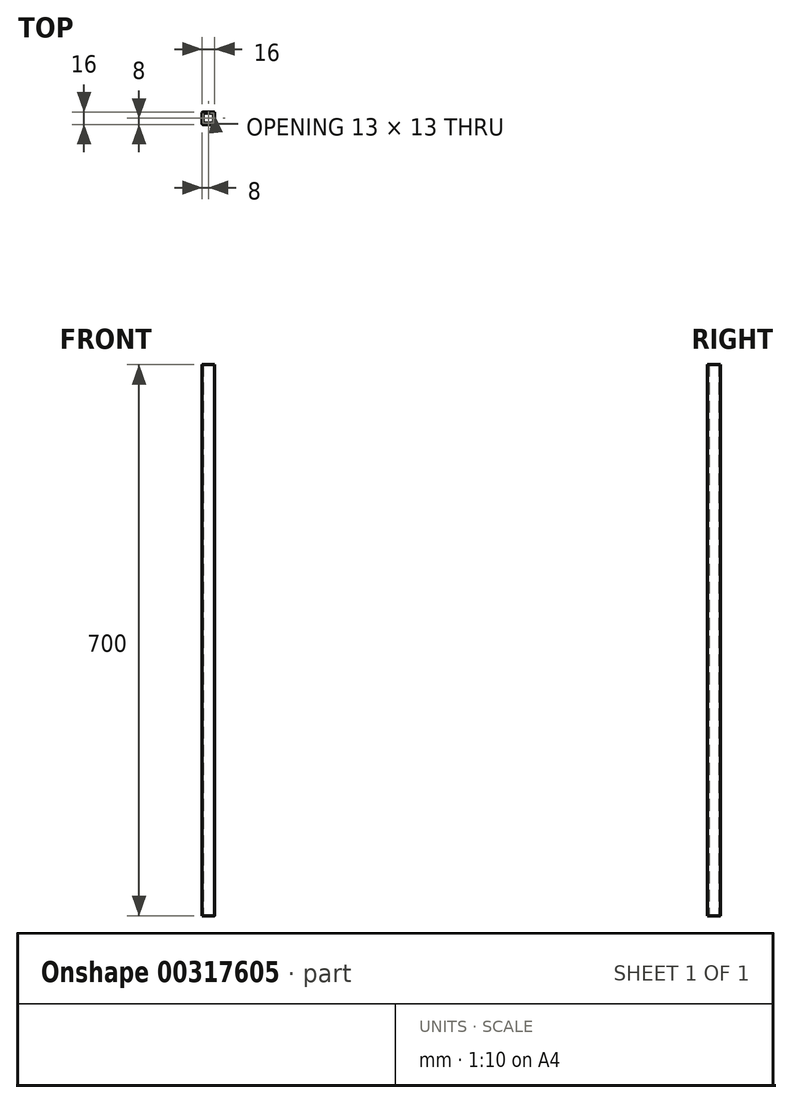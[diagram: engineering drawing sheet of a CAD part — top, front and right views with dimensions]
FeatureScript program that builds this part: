
annotation { "Feature Type Name" : "Feature", "Feature Type Description" : "" }
export const myFeature = defineFeature(function(context is Context, id is Id, definition is map)
    precondition{}
    {
        {
            var Q0;
            Q0=qCreatedBy(makeId("Top.planeOp"),FACE);
            var sketch = newSketch(context, id + "F0", { "sketchPlane" : qUnion([Q0])});
            skLineSegment(sketch, "E0.bottom", {"start": v(-8, -8) * mm, "end": v(8, -8) * mm});
            skLineSegment(sketch, "E0.top", {"start": v(-8, 8) * mm, "end": v(8, 8) * mm});
            skLineSegment(sketch, "E0.left", {"start": v(-8, -8) * mm, "end": v(-8, 8) * mm});
            skLineSegment(sketch, "E0.right", {"start": v(8, -8) * mm, "end": v(8, 8) * mm});
            skSolve(sketch);
        }
        {
            var Q0;
            Q0=makeQuery(id+"F0.imprint","IMPRINT",FACE,{"disambiguationData":[TD([[makeQuery(id+"F0.imprint","IMPRINT",EDGE,{"derivedFrom":sQuery(id+"F0.wireOp",EDGE,"E0.bottom")}),1.0]])]});
            extrude(context, id + "F1", {"entities" : qUnion([Q0]), "depth" : 700 * mm});
        }
        {
            var Q0;
            Q0=makeQuery(id+"F1.opExtrude","CAP_FACE",FACE,{"disambiguationData":[OSD([sQuery(id+"F0.wireOp",EDGE,"E0.bottom"),sQuery(id+"F0.wireOp",EDGE,"E0.top"),sQuery(id+"F0.wireOp",EDGE,"E0.left"),sQuery(id+"F0.wireOp",EDGE,"E0.right")])],"isStart":false});
            var Q1;
            Q1=makeQuery(id+"F1.opExtrude","CAP_FACE",FACE,{"disambiguationData":[OSD([sQuery(id+"F0.wireOp",EDGE,"E0.bottom"),sQuery(id+"F0.wireOp",EDGE,"E0.top"),sQuery(id+"F0.wireOp",EDGE,"E0.left"),sQuery(id+"F0.wireOp",EDGE,"E0.right")])],"isStart":true});
            shell(context, id + "F2", {"entities" : qUnion([Q0, Q1]), "thickness" : 1.5 * mm});
        }
        {
            var Q0;
            Q0=makeQuery(id+"F1.opExtrude","SWEPT_EDGE",EDGE,{"disambiguationData":[OSD([sQuery(id+"F0.wireOp",EDGE,"E0.top"),sQuery(id+"F0.wireOp",EDGE,"E0.left")])]});
            var Q1;
            Q1=makeQuery(id+"F1.opExtrude","SWEPT_EDGE",EDGE,{"disambiguationData":[OSD([sQuery(id+"F0.wireOp",EDGE,"E0.top"),sQuery(id+"F0.wireOp",EDGE,"E0.right")])]});
            var Q2;
            Q2=makeQuery(id+"F1.opExtrude","SWEPT_EDGE",EDGE,{"disambiguationData":[OSD([sQuery(id+"F0.wireOp",EDGE,"E0.bottom"),sQuery(id+"F0.wireOp",EDGE,"E0.right")])]});
            var Q3;
            Q3=makeQuery(id+"F1.opExtrude","SWEPT_EDGE",EDGE,{"disambiguationData":[OSD([sQuery(id+"F0.wireOp",EDGE,"E0.bottom"),sQuery(id+"F0.wireOp",EDGE,"E0.left")])]});
            fillet(context, id + "F3", {"entities" : qUnion([Q0, Q1, Q2, Q3]), "radius" : 1.5 * mm, "tangentPropagation" : true, "allowEdgeOverflow" : false});
        }
        {
            var Q0;
            Q0=makeQuery(id+"F2.opShell","OFFSET_EDGE",EDGE,{"disambiguationData":[OSD([sQuery(id+"F0.wireOp",EDGE,"E0.top"),sQuery(id+"F0.wireOp",EDGE,"E0.right")])]});
            var Q1;
            Q1=makeQuery(id+"F2.opShell","OFFSET_EDGE",EDGE,{"disambiguationData":[OSD([sQuery(id+"F0.wireOp",EDGE,"E0.top"),sQuery(id+"F0.wireOp",EDGE,"E0.left")])]});
            var Q2;
            Q2=makeQuery(id+"F2.opShell","OFFSET_EDGE",EDGE,{"disambiguationData":[OSD([sQuery(id+"F0.wireOp",EDGE,"E0.bottom"),sQuery(id+"F0.wireOp",EDGE,"E0.left")])]});
            var Q3;
            Q3=makeQuery(id+"F2.opShell","OFFSET_EDGE",EDGE,{"disambiguationData":[OSD([sQuery(id+"F0.wireOp",EDGE,"E0.bottom"),sQuery(id+"F0.wireOp",EDGE,"E0.right")])]});
            fillet(context, id + "F4", {"entities" : qUnion([Q0, Q1, Q2, Q3]), "radius" : 1 * mm, "tangentPropagation" : true, "allowEdgeOverflow" : false});
        }
    });
